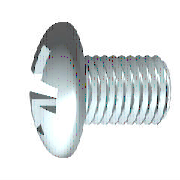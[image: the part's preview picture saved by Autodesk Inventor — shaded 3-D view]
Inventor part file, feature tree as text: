
AUTODESK INVENTOR PART (.ipt)
format: ipt  version: 2020.2 (Build 242310000, 310)  size: 261,120 bytes
history: native  units: mm (DEFAULTED — no unit token found)
features: extrude x1, other x1, plane x1
ambient origin geometry x7: Origin, YZ Plane, XZ Plane, X Axis, Y Axis, Z Axis, Center Point
bodies: Solid1 (feature_tree), Body (feature_tree)
feature tree (3):
  extrude  "Slot"  Depth=3.0mm
  other  "Cut"
  plane  "Work Plane3"
